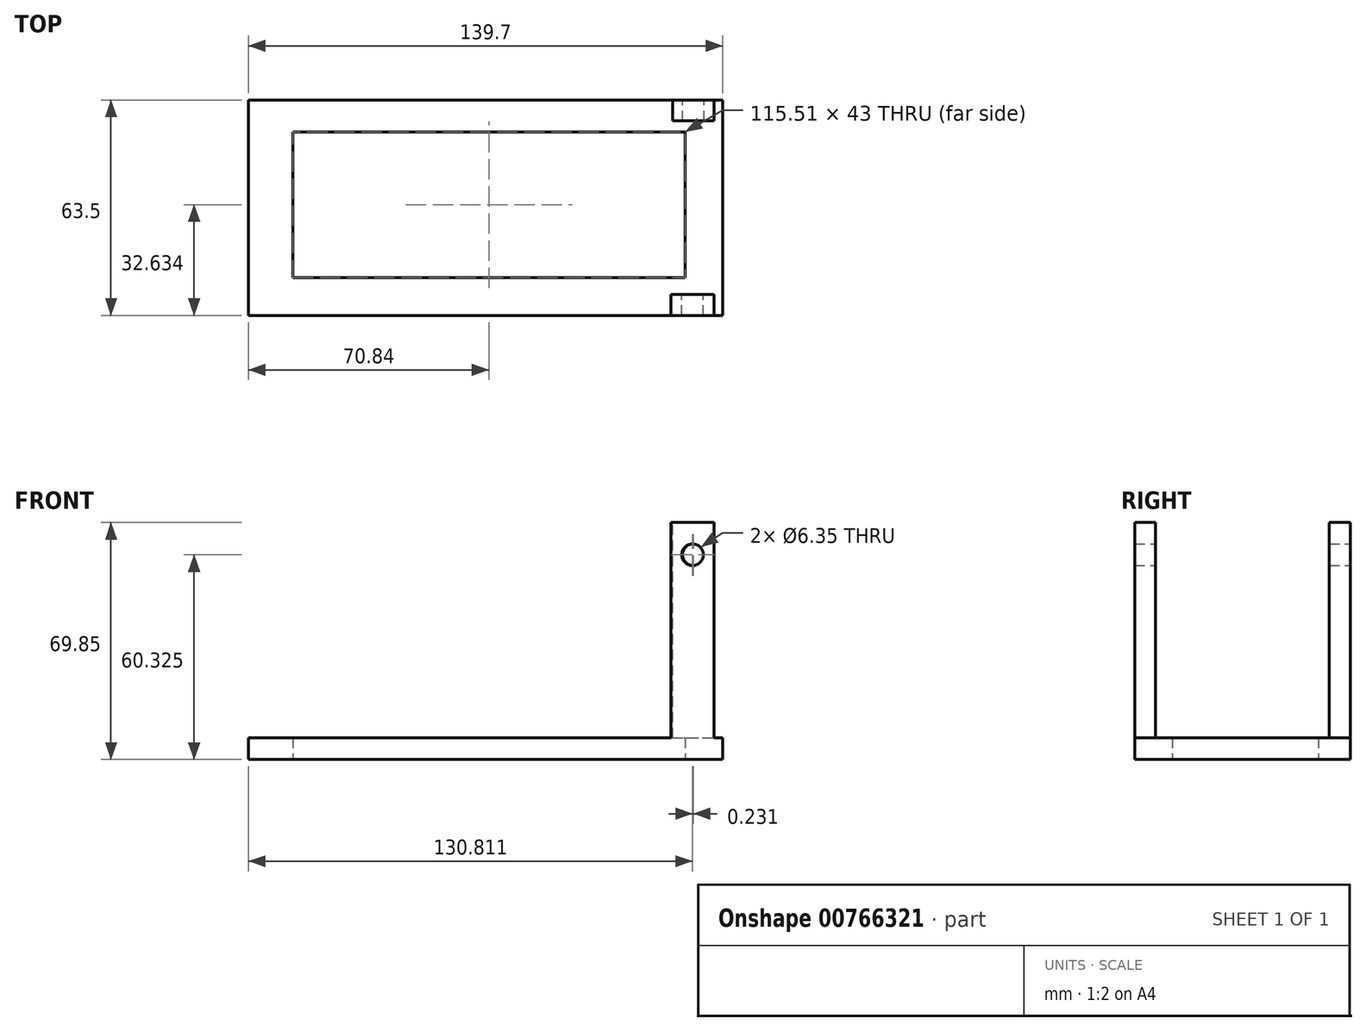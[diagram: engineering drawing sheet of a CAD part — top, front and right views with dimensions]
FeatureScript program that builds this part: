
annotation { "Feature Type Name" : "Feature", "Feature Type Description" : "" }
export const myFeature = defineFeature(function(context is Context, id is Id, definition is map)
    precondition{}
    {
        {
            var Q0;
            Q0=qCreatedBy(makeId("Top.planeOp"),FACE);
            var sketch = newSketch(context, id + "F0", { "sketchPlane" : qUnion([Q0])});
            skLineSegment(sketch, "E0.bottom", {"start": v(-88.02, -40.49) * mm, "end": v(51.68, -40.49) * mm});
            skLineSegment(sketch, "E0.top", {"start": v(-88.02, 23.01) * mm, "end": v(51.68, 23.01) * mm});
            skLineSegment(sketch, "E0.left", {"start": v(-88.02, -40.49) * mm, "end": v(-88.02, 23.01) * mm});
            skLineSegment(sketch, "E0.right", {"start": v(51.68, -40.49) * mm, "end": v(51.68, 23.01) * mm});
            skLineSegment(sketch, "E1.bottom", {"start": v(-74.93, -29.36) * mm, "end": v(40.57, -29.36) * mm});
            skLineSegment(sketch, "E1.top", {"start": v(-74.93, 13.65) * mm, "end": v(40.57, 13.65) * mm});
            skLineSegment(sketch, "E1.left", {"start": v(-74.93, -29.36) * mm, "end": v(-74.93, 13.65) * mm});
            skLineSegment(sketch, "E1.right", {"start": v(40.57, -29.36) * mm, "end": v(40.57, 13.65) * mm});
            skSolve(sketch);
        }
        {
            var Q0;
            Q0=makeQuery(id+"F0.imprint","IMPRINT",FACE,{"disambiguationData":[TD([[makeQuery(id+"F0.imprint","IMPRINT",EDGE,{"derivedFrom":sQuery(id+"F0.wireOp",EDGE,"E0.bottom")}),1.0]])]});
            extrude(context, id + "F1", {"entities" : qUnion([Q0]), "depth" : 6.35 * mm, "offsetDistance" : 25.4 * mm});
        }
        {
            var Q0;
            Q0=makeQuery(id+"F1.opExtrude","SWEPT_FACE",FACE,{"disambiguationData":[OSD([sQuery(id+"F0.wireOp",EDGE,"E0.bottom")])]});
            var sketch = newSketch(context, id + "F2", { "sketchPlane" : qUnion([Q0])});
            skLineSegment(sketch, "E2.bottom", {"start": v(49.14, 6.35) * mm, "end": v(36.44, 6.35) * mm});
            skLineSegment(sketch, "E2.top", {"start": v(49.14, 69.85) * mm, "end": v(36.44, 69.85) * mm});
            skLineSegment(sketch, "E2.left", {"start": v(49.14, 6.35) * mm, "end": v(49.14, 69.85) * mm});
            skLineSegment(sketch, "E2.right", {"start": v(36.44, 6.35) * mm, "end": v(36.44, 69.85) * mm});
            skSolve(sketch);
        }
        {
            var Q0;
            Q0 = qSketchRegion(id + "F2", true);
            extrude(context, id + "F3", {"entities" : qUnion([Q0]), "operationType" : NewBodyOperationType.ADD, "oppositeDirection" : true, "depth" : 6.17 * mm, "offsetDistance" : 25.4 * mm});
        }
        {
            var Q0;
            Q0=makeQuery(id+"F3.opExtrude","CAP_FACE",FACE,{"disambiguationData":[OSD([sQuery(id+"F2.wireOp",EDGE,"E2.bottom"),sQuery(id+"F2.wireOp",EDGE,"E2.top"),sQuery(id+"F2.wireOp",EDGE,"E2.left"),sQuery(id+"F2.wireOp",EDGE,"E2.right")])],"isStart":false});
            var sketch = newSketch(context, id + "F4", { "sketchPlane" : qUnion([Q0])});
            skCircle(sketch, "E3", {"center": v(-42.8, 60.32) * mm, "radius": 3.18 * mm});
            skPoint(sketch, "E3.centerSnap0", {"position": v(-42.8, 69.85) * mm});
            skSolve(sketch);
        }
        {
            var Q0;
            Q0 = qSketchRegion(id + "F4", true);
            extrude(context, id + "F5", {"entities" : qUnion([Q0]), "operationType" : NewBodyOperationType.REMOVE, "oppositeDirection" : true, "depth" : 32.64 * mm, "offsetDistance" : 25.4 * mm});
        }
        {
            var Q0;
            Q0=makeQuery(id+"F1.opExtrude","SWEPT_FACE",FACE,{"disambiguationData":[OSD([sQuery(id+"F0.wireOp",EDGE,"E0.top")])]});
            var sketch = newSketch(context, id + "F6", { "sketchPlane" : qUnion([Q0])});
            skLineSegment(sketch, "E4.bottom", {"start": v(-49.14, 6.35) * mm, "end": v(-36.9, 6.35) * mm});
            skLineSegment(sketch, "E4.top", {"start": v(-49.14, 69.85) * mm, "end": v(-36.9, 69.85) * mm});
            skLineSegment(sketch, "E4.left", {"start": v(-49.14, 6.35) * mm, "end": v(-49.14, 69.85) * mm});
            skLineSegment(sketch, "E4.right", {"start": v(-36.9, 6.35) * mm, "end": v(-36.9, 69.85) * mm});
            skSolve(sketch);
        }
        {
            var Q0;
            Q0 = qSketchRegion(id + "F6", true);
            extrude(context, id + "F7", {"entities" : qUnion([Q0]), "operationType" : NewBodyOperationType.ADD, "oppositeDirection" : true, "depth" : 6.17 * mm, "offsetDistance" : 25.4 * mm});
        }
        {
            var Q0;
            Q0=makeQuery(id+"F7.boolean.opBoolean","MERGE",FACE,{"derivedFrom":[makeQuery(id+"F1.opExtrude","SWEPT_FACE",FACE,{"disambiguationData":[OSD([sQuery(id+"F0.wireOp",EDGE,"E0.top")])]}),makeQuery(id+"F7.opExtrude","CAP_FACE",FACE,{"disambiguationData":[OSD([sQuery(id+"F6.wireOp",EDGE,"E4.bottom"),sQuery(id+"F6.wireOp",EDGE,"E4.top"),sQuery(id+"F6.wireOp",EDGE,"E4.left"),sQuery(id+"F6.wireOp",EDGE,"E4.right")])],"isStart":true})]});
            var sketch = newSketch(context, id + "F8", { "sketchPlane" : qUnion([Q0])});
            skCircle(sketch, "E5", {"center": v(-43.02, 60.32) * mm, "radius": 3.18 * mm});
            skPoint(sketch, "E5.centerSnap0", {"position": v(-43.02, 69.85) * mm});
            skSolve(sketch);
        }
        {
            var Q0;
            Q0=makeQuery(id+"F8.imprint","IMPRINT",FACE,{"disambiguationData":[TD([[makeQuery(id+"F8.imprint","IMPRINT",EDGE,{"derivedFrom":sQuery(id+"F8.wireOp",EDGE,"E5")}),1.0]])]});
            extrude(context, id + "F9", {"entities" : qUnion([Q0]), "operationType" : NewBodyOperationType.REMOVE, "oppositeDirection" : true, "depth" : 25.4 * mm, "offsetDistance" : 25.4 * mm});
        }
    });
